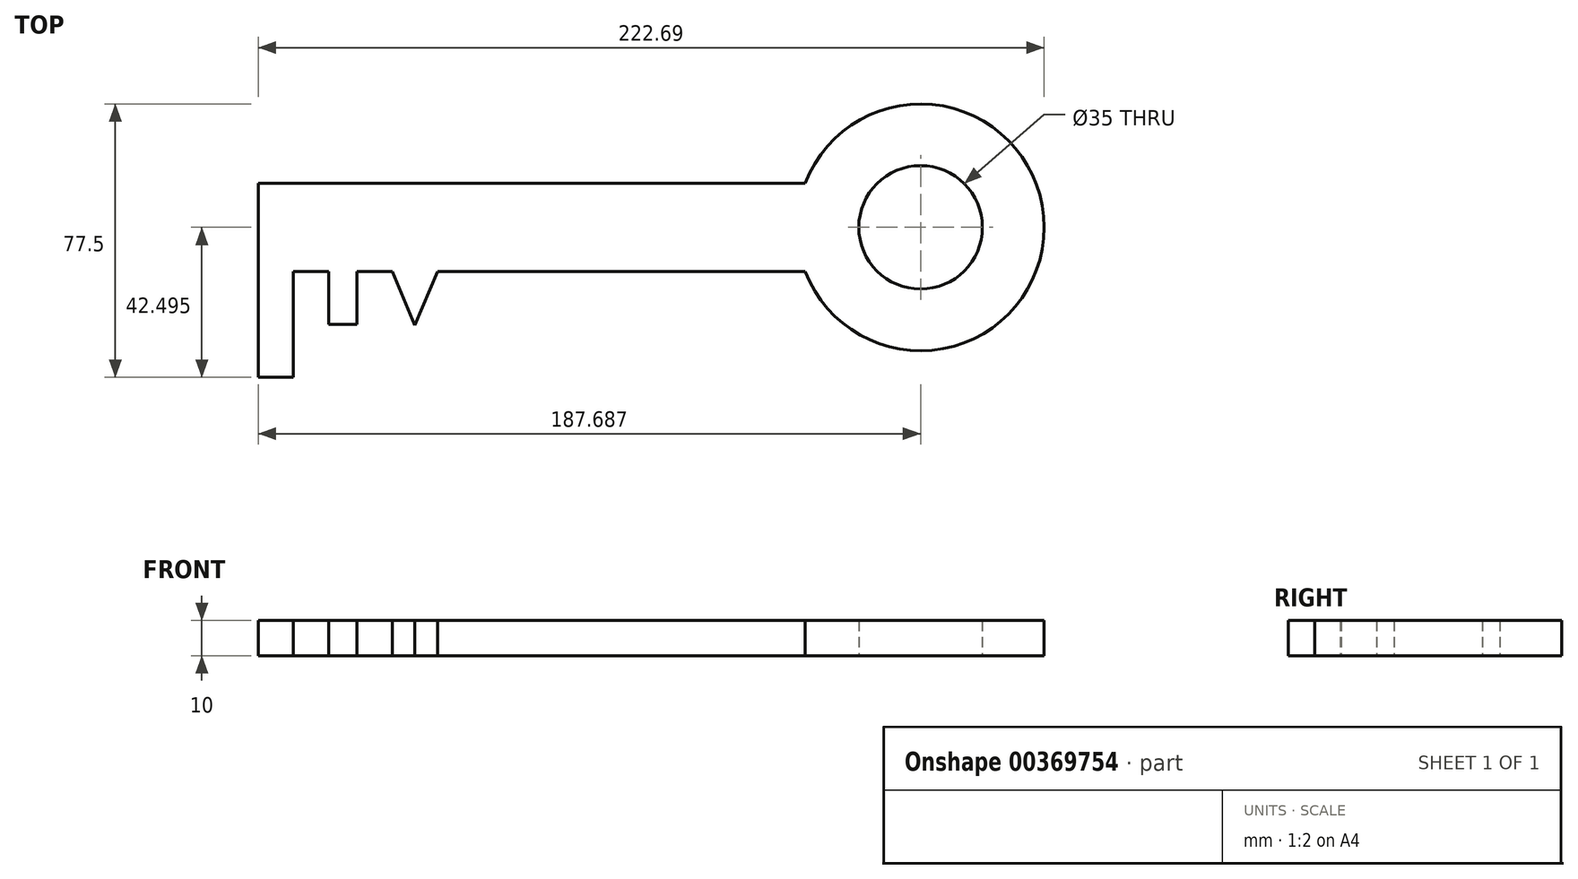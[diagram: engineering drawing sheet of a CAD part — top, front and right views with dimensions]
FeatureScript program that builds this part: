
annotation { "Feature Type Name" : "Feature", "Feature Type Description" : "" }
export const myFeature = defineFeature(function(context is Context, id is Id, definition is map)
    precondition{}
    {
        {
            var Q0;
            Q0=qCreatedBy(makeId("Top.planeOp"),FACE);
            var sketch = newSketch(context, id + "F0", { "sketchPlane" : qUnion([Q0])});
            skLineSegment(sketch, "E0.bottom", {"start": v(-105.3, 12.38) * mm, "end": v(49.7, 12.38) * mm});
            skLineSegment(sketch, "E0.top", {"start": v(-95.3, -12.62) * mm, "end": v(-85.3, -12.62) * mm});
            skLineSegment(sketch, "E0.left", {"start": v(-105.3, 12.38) * mm, "end": v(-105.3, -12.62) * mm});
            skLineSegment(sketch, "E1.top", {"start": v(-105.3, -42.62) * mm, "end": v(-95.3, -42.62) * mm});
            skLineSegment(sketch, "E1.left", {"start": v(-105.3, -12.62) * mm, "end": v(-105.3, -42.62) * mm});
            skLineSegment(sketch, "E1.right", {"start": v(-95.3, -12.62) * mm, "end": v(-95.3, -42.62) * mm});
            skLineSegment(sketch, "E2.top", {"start": v(-85.3, -27.62) * mm, "end": v(-77.3, -27.62) * mm});
            skLineSegment(sketch, "E2.left", {"start": v(-85.3, -12.62) * mm, "end": v(-85.3, -27.62) * mm});
            skLineSegment(sketch, "E2.right", {"start": v(-77.3, -12.62) * mm, "end": v(-77.3, -27.62) * mm});
            skLineSegment(sketch, "E3", {"start": v(-67.3, -12.62) * mm, "end": v(-60.87, -27.88) * mm});
            skLineSegment(sketch, "E4", {"start": v(-60.87, -27.88) * mm, "end": v(-54.44, -12.62) * mm});
            skLineSegment(sketch, "E5", {"start": v(-77.3, -12.62) * mm, "end": v(-67.3, -12.62) * mm});
            skArc(sketch, "E6", {"start": v(49.7, -12.62) * mm, "mid": v(117.4, -0.12) * mm, "end": v(49.7, 12.38) * mm});
            skCircle(sketch, "E7", {"center": v(82.4, -0.12) * mm, "radius": 17.5 * mm});
            skLineSegment(sketch, "E8", {"start": v(82.4, -0.12) * mm, "end": v(-105.3, -0.12) * mm, "construction": true});
            skLineSegment(sketch, "E9.trimOffspring", {"start": v(-54.44, -12.62) * mm, "end": v(49.7, -12.62) * mm});
            skSolve(sketch);
        }
        {
            var Q0;
            Q0=makeQuery(id+"F0.imprint","IMPRINT",FACE,{"disambiguationData":[TD([[makeQuery(id+"F0.imprint","IMPRINT",EDGE,{"derivedFrom":sQuery(id+"F0.wireOp",EDGE,"E0.bottom")}),-1.0]])]});
            extrude(context, id + "F1", {"entities" : qUnion([Q0]), "depth" : 10 * mm});
        }
    });
